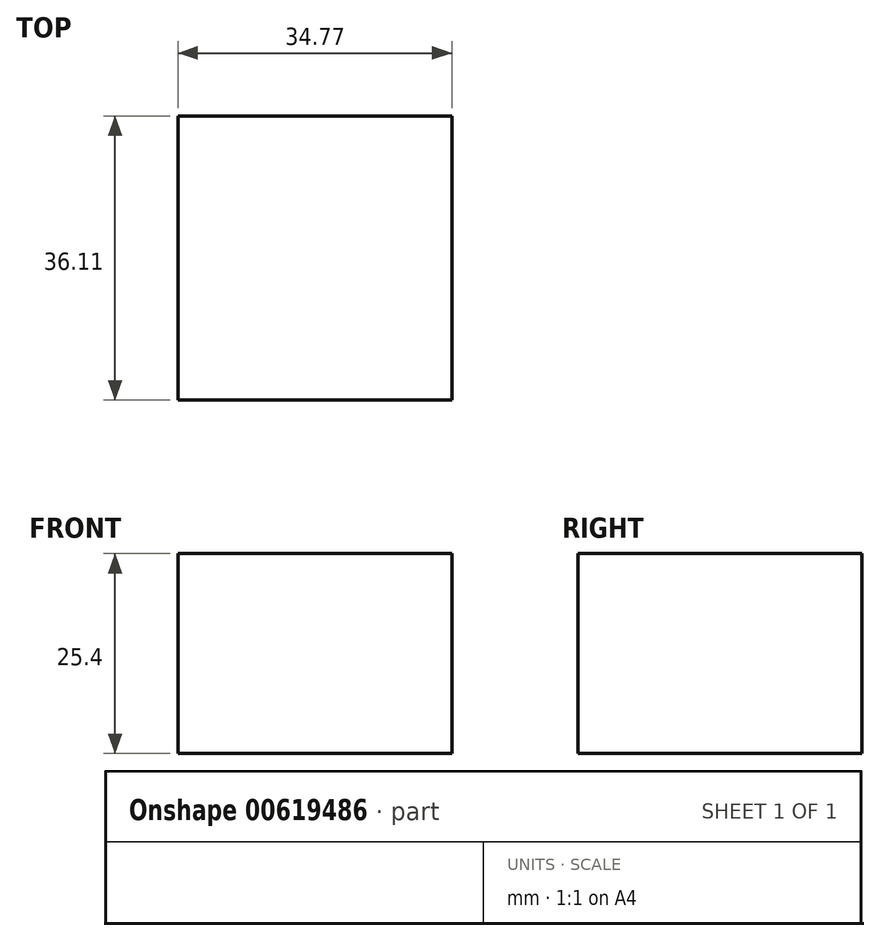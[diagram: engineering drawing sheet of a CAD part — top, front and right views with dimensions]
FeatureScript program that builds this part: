
annotation { "Feature Type Name" : "Feature", "Feature Type Description" : "" }
export const myFeature = defineFeature(function(context is Context, id is Id, definition is map)
    precondition{}
    {
        {
            var Q0;
            Q0=qCreatedBy(makeId("Top.planeOp"),FACE);
            var sketch = newSketch(context, id + "F0", { "sketchPlane" : qUnion([Q0])});
            skLineSegment(sketch, "E0.bottom", {"start": v(-14.49, 11.81) * mm, "end": v(20.28, 11.81) * mm});
            skLineSegment(sketch, "E0.top", {"start": v(-14.49, -24.3) * mm, "end": v(20.28, -24.3) * mm});
            skLineSegment(sketch, "E0.left", {"start": v(-14.49, 11.81) * mm, "end": v(-14.49, -24.3) * mm});
            skLineSegment(sketch, "E0.right", {"start": v(20.28, 11.81) * mm, "end": v(20.28, -24.3) * mm});
            skSolve(sketch);
        }
        {
            var Q0;
            Q0=makeQuery(id+"F0.imprint","IMPRINT",FACE,{"disambiguationData":[TD([[makeQuery(id+"F0.imprint","IMPRINT",EDGE,{"derivedFrom":sQuery(id+"F0.wireOp",EDGE,"E0.bottom")}),-1.0]])]});
            extrude(context, id + "F1", {"entities" : qUnion([Q0]), "depth" : 25.4 * mm, "offsetDistance" : 25.4 * mm});
        }
    });
